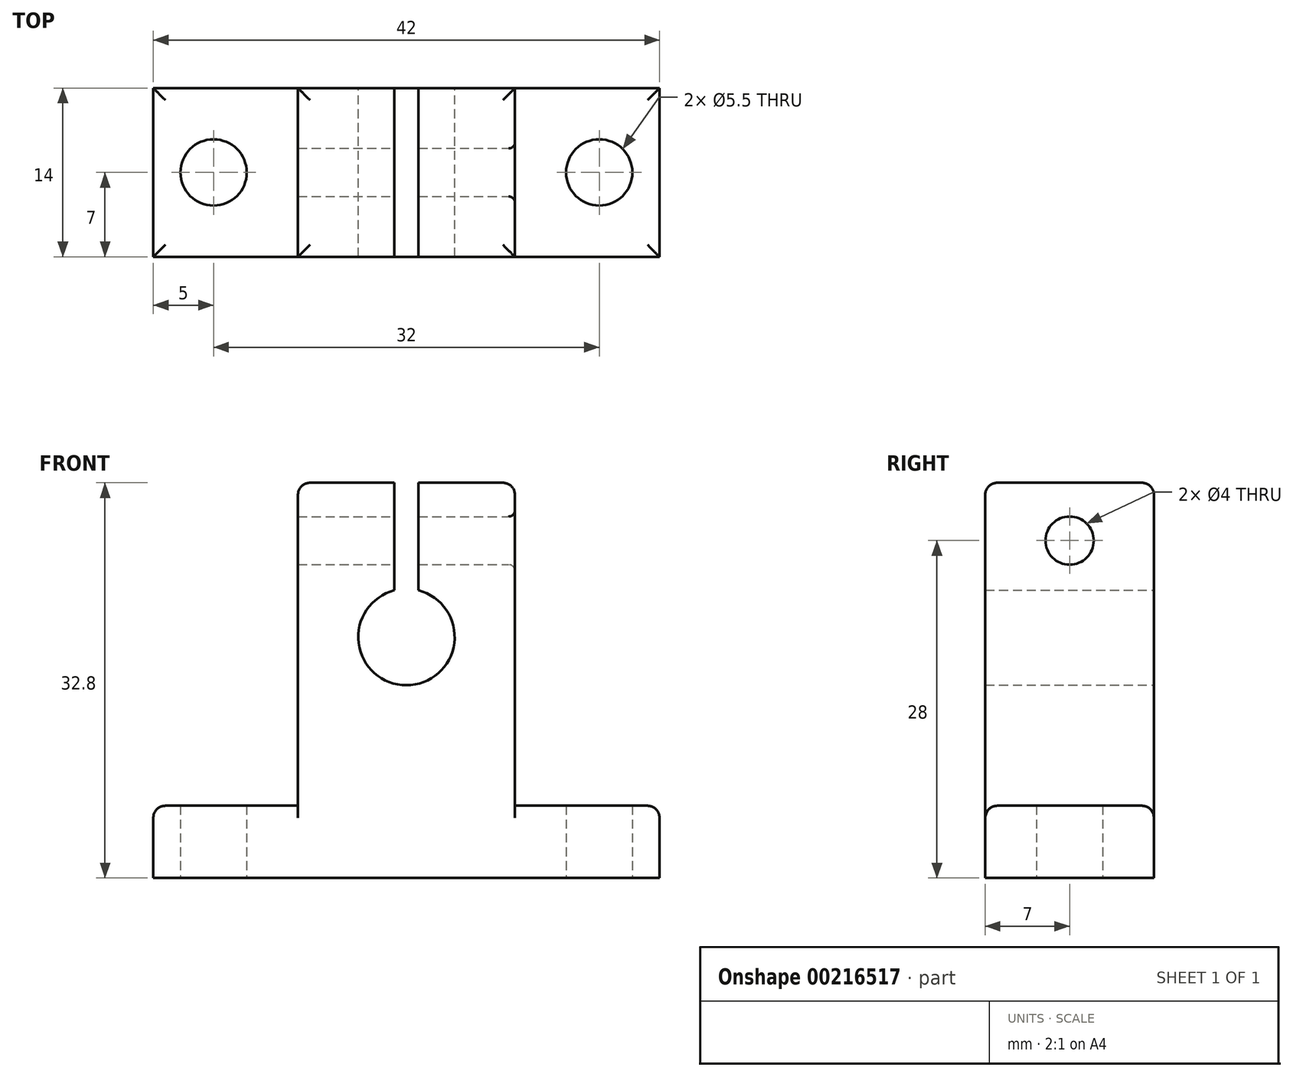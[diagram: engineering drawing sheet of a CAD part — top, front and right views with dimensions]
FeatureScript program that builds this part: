
annotation { "Feature Type Name" : "Feature", "Feature Type Description" : "" }
export const myFeature = defineFeature(function(context is Context, id is Id, definition is map)
    precondition{}
    {
        {
            var Q0;
            Q0=qCreatedBy(makeId("Front.planeOp"),FACE);
            var sketch = newSketch(context, id + "F0", { "sketchPlane" : qUnion([Q0])});
            skLineSegment(sketch, "E0.bottom", {"start": v(-21, 6) * mm, "end": v(-9, 6) * mm});
            skLineSegment(sketch, "E0.top", {"start": v(-21, 0) * mm, "end": v(21, 0) * mm});
            skLineSegment(sketch, "E0.left", {"start": v(-21, 6) * mm, "end": v(-21, 0) * mm});
            skLineSegment(sketch, "E0.right", {"start": v(21, 6) * mm, "end": v(21, 0) * mm});
            skLineSegment(sketch, "E1.bottom", {"start": v(-9, 32.8) * mm, "end": v(-1, 32.8) * mm});
            skLineSegment(sketch, "E1.left", {"start": v(-9, 32.8) * mm, "end": v(-9, 6) * mm});
            skLineSegment(sketch, "E1.right", {"start": v(9, 32.8) * mm, "end": v(9, 6) * mm});
            skPoint(sketch, "E2", {"position": v(-9, 6) * mm});
            skPoint(sketch, "E3", {"position": v(9, 6) * mm});
            skLineSegment(sketch, "E4.trimOffspring", {"start": v(9, 6) * mm, "end": v(21, 6) * mm});
            skLineSegment(sketch, "E5", {"start": v(-26.53, 20) * mm, "end": v(25.47, 20) * mm, "construction": true});
            skLineSegment(sketch, "E6", {"start": v(0, 47.77) * mm, "end": v(0, -24.77) * mm, "construction": true});
            skPoint(sketch, "E7", {"position": v(0, 20) * mm});
            skArc(sketch, "E8", {"start": v(-1, 23.87) * mm, "mid": v(0, 16) * mm, "end": v(1, 23.87) * mm});
            skLineSegment(sketch, "E9", {"start": v(-1, 32.8) * mm, "end": v(-1, 23.87) * mm});
            skLineSegment(sketch, "E10", {"start": v(1, 32.8) * mm, "end": v(1, 23.87) * mm});
            skLineSegment(sketch, "E11.trimOffspring", {"start": v(1, 32.8) * mm, "end": v(9, 32.8) * mm});
            skSolve(sketch);
        }
        {
            var Q0;
            Q0=makeQuery(id+"F0.imprint","IMPRINT",FACE,{"disambiguationData":[TD([[makeQuery(id+"F0.imprint","IMPRINT",EDGE,{"derivedFrom":sQuery(id+"F0.wireOp",EDGE,"E0.bottom")}),-1.0]])]});
            extrude(context, id + "F1", {"entities" : qUnion([Q0]), "depth" : 14 * mm});
        }
        {
            var Q0;
            Q0=qCreatedBy(makeId("Top.planeOp"),FACE);
            var sketch = newSketch(context, id + "F2", { "sketchPlane" : qUnion([Q0])});
            skLineSegment(sketch, "E12", {"start": v(-26.72, -7) * mm, "end": v(28.4, -7) * mm, "construction": true});
            skLineSegment(sketch, "E13", {"start": v(-16, 7.27) * mm, "end": v(-16, -22.73) * mm, "construction": true});
            skLineSegment(sketch, "E14", {"start": v(16, 4.5) * mm, "end": v(16, -25.5) * mm, "construction": true});
            skPoint(sketch, "E15", {"position": v(-16, -7) * mm});
            skPoint(sketch, "E16", {"position": v(16, -7) * mm});
            skCircle(sketch, "E17", {"center": v(-16, -7) * mm, "radius": 2.75 * mm});
            skCircle(sketch, "E18", {"center": v(16, -7) * mm, "radius": 2.75 * mm});
            skSolve(sketch);
        }
        {
            var Q0;
            Q0=makeQuery(id+"F2.imprint","IMPRINT",FACE,{"disambiguationData":[TD([[makeQuery(id+"F2.imprint","IMPRINT",EDGE,{"derivedFrom":sQuery(id+"F2.wireOp",EDGE,"E18")}),1.0]])]});
            var Q1;
            Q1=makeQuery(id+"F2.imprint","IMPRINT",FACE,{"disambiguationData":[TD([[makeQuery(id+"F2.imprint","IMPRINT",EDGE,{"derivedFrom":sQuery(id+"F2.wireOp",EDGE,"E17")}),1.0]])]});
            extrude(context, id + "F3", {"entities" : qUnion([Q0, Q1]), "operationType" : NewBodyOperationType.REMOVE, "depth" : 6 * mm});
        }
        {
            var Q0;
            Q0=makeQuery(id+"F1.opExtrude","SWEPT_EDGE",EDGE,{"disambiguationData":[OSD([sQuery(id+"F0.wireOp",EDGE,"E0.bottom"),sQuery(id+"F0.wireOp",EDGE,"E0.left")])]});
            var Q1;
            Q1=makeQuery(id+"F1.opExtrude","CAP_EDGE",EDGE,{"disambiguationData":[OSD([sQuery(id+"F0.wireOp",EDGE,"E0.bottom")])],"isStart":true});
            var Q2;
            Q2=makeQuery(id+"F1.opExtrude","CAP_EDGE",EDGE,{"disambiguationData":[OSD([sQuery(id+"F0.wireOp",EDGE,"E0.bottom")])],"isStart":false});
            var Q3;
            Q3=makeQuery(id+"F1.opExtrude","CAP_EDGE",EDGE,{"disambiguationData":[OSD([sQuery(id+"F0.wireOp",EDGE,"E4.trimOffspring")])],"isStart":false});
            var Q4;
            Q4=makeQuery(id+"F1.opExtrude","SWEPT_EDGE",EDGE,{"disambiguationData":[OSD([sQuery(id+"F0.wireOp",EDGE,"E0.right"),sQuery(id+"F0.wireOp",EDGE,"E4.trimOffspring")])]});
            var Q5;
            Q5=makeQuery(id+"F1.opExtrude","CAP_EDGE",EDGE,{"disambiguationData":[OSD([sQuery(id+"F0.wireOp",EDGE,"E4.trimOffspring")])],"isStart":true});
            var Q6;
            Q6=makeQuery(id+"F1.opExtrude","SWEPT_EDGE",EDGE,{"disambiguationData":[OSD([sQuery(id+"F0.wireOp",EDGE,"E1.bottom"),sQuery(id+"F0.wireOp",EDGE,"E1.left")])]});
            var Q7;
            Q7=makeQuery(id+"F1.opExtrude","SWEPT_EDGE",EDGE,{"disambiguationData":[OSD([sQuery(id+"F0.wireOp",EDGE,"E1.right"),sQuery(id+"F0.wireOp",EDGE,"E11.trimOffspring")])]});
            var Q8;
            Q8=makeQuery(id+"F1.opExtrude","CAP_EDGE",EDGE,{"disambiguationData":[OSD([sQuery(id+"F0.wireOp",EDGE,"E11.trimOffspring")])],"isStart":true});
            var Q9;
            Q9=makeQuery(id+"F1.opExtrude","CAP_EDGE",EDGE,{"disambiguationData":[OSD([sQuery(id+"F0.wireOp",EDGE,"E1.bottom")])],"isStart":true});
            var Q10;
            Q10=makeQuery(id+"F1.opExtrude","CAP_EDGE",EDGE,{"disambiguationData":[OSD([sQuery(id+"F0.wireOp",EDGE,"E1.bottom")])],"isStart":false});
            var Q11;
            Q11=makeQuery(id+"F1.opExtrude","CAP_EDGE",EDGE,{"disambiguationData":[OSD([sQuery(id+"F0.wireOp",EDGE,"E11.trimOffspring")])],"isStart":false});
            fillet(context, id + "F4", {"entities" : qUnion([Q0, Q1, Q2, Q3, Q4, Q5, Q6, Q7, Q8, Q9, Q10, Q11]), "radius" : 1 * mm, "tangentPropagation" : true, "allowEdgeOverflow" : false});
        }
        {
            var Q0;
            Q0=qCreatedBy(makeId("Right.planeOp"),FACE);
            var sketch = newSketch(context, id + "F5", { "sketchPlane" : qUnion([Q0])});
            skLineSegment(sketch, "E19", {"start": v(-7, 40.06) * mm, "end": v(-7, -6.67) * mm, "construction": true});
            skLineSegment(sketch, "E20", {"start": v(-18.45, 28) * mm, "end": v(2.78, 28) * mm, "construction": true});
            skCircle(sketch, "E21", {"center": v(-7, 28) * mm, "radius": 2 * mm});
            skSolve(sketch);
        }
        {
            var Q0;
            Q0=qSketchRegion(id+"F5",true);
            var Q1;
            Q1=sQuery(id+"F5.wireOp",EDGE,"E21");
            extrude(context, id + "F6", {"entities" : qUnion([Q0]), "operationType" : NewBodyOperationType.REMOVE, "surfaceEntities" : qUnion([Q1]), "oppositeDirection" : true, "depth" : 10 * mm, "hasSecondDirection" : true, "secondDirectionOppositeDirection" : false, "secondDirectionDepth" : 9 * mm});
        }
        {
            var Q0;
            Q0=makeQuery(id+"F6.boolean.opBoolean","INTERSECT",EDGE,{"derivedFrom":[makeQuery(id+"F1.opExtrude","SWEPT_FACE",FACE,{"disambiguationData":[OSD([sQuery(id+"F0.wireOp",EDGE,"E1.right")])]}),makeQuery(id+"F6.opExtrude","SWEPT_FACE",FACE,{"disambiguationData":[OSD([sQuery(id+"F5.wireOp",EDGE,"E21")])]})]});
            fillet(context, id + "F7", {"entities" : qUnion([Q0]), "radius" : .5 * mm, "tangentPropagation" : true, "allowEdgeOverflow" : false});
        }
    });
